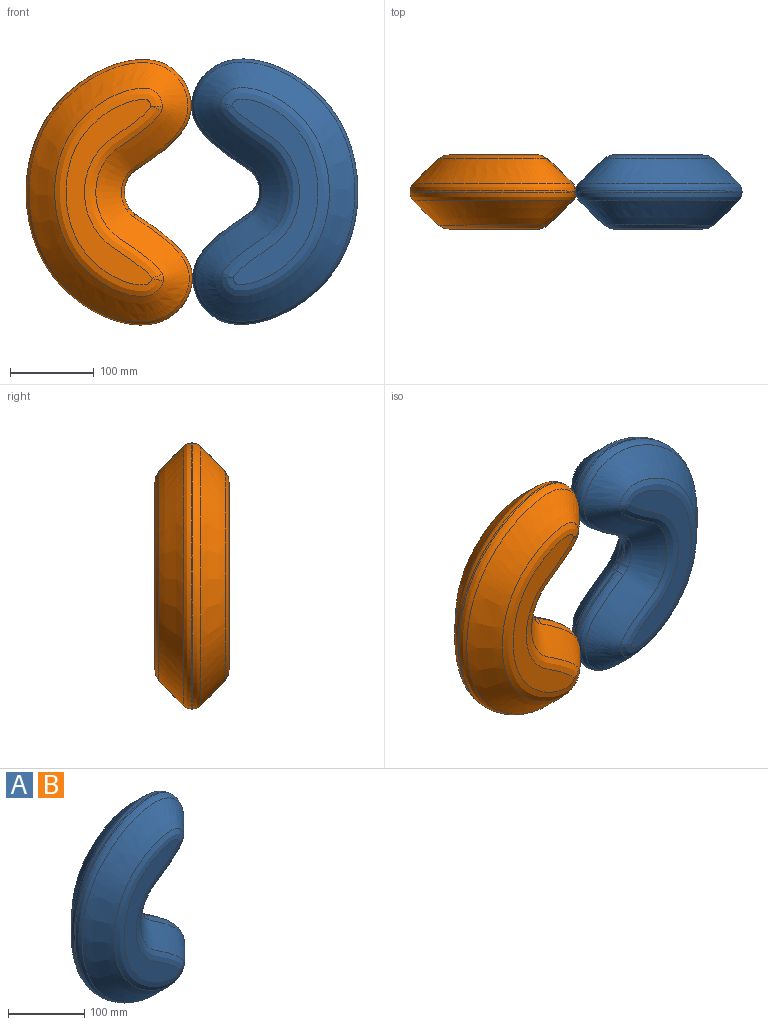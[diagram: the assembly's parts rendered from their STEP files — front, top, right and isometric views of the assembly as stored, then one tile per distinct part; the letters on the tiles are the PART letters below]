
ASSEMBLY  parts=2 mates=1
PART A: 24 faces, bbox 198.6x88.9x316.7 mm
  f0: plane 221.21x102.81mm, normal (0,-1,0), area 7218.9mm2, adj f3,f4
  f1: bspline ~309.04x190.25mm, area 33901.5mm2, adj f2,f3,f4,f5,f20,f21,f22,f23
  f2: bspline ~13.73x8.65mm, area 69mm2, adj f1,f3,f4
  f3: bspline ~206.74x93.09mm, area 3926.4mm2, adj f0,f1,f2,f5
  f4: bspline ~248.24x129.72mm, area 5664.5mm2, adj f0,f1,f2,f5
  f5: bspline ~13.51x5.1mm, area 25.1mm2, adj f1,f3,f4
  f6: cylinder r=25.4mm len=7.28mm, axis (0,-1,0), area 21.9mm2, adj f7,f9,f17,f22
  f7: extruded ~315.96x197.64mm, area 1742.8mm2, adj f6,f8,f16,f20
  f8: cylinder r=25.4mm len=7.32mm, axis (0,-1,0), area 22mm2, adj f7,f9,f18,f21
  f9: cylinder r=34.34mm len=37.54mm, axis (0,-1,0), area 84mm2, adj f6,f8,f19,f23
  f10: plane 221.21x102.81mm, normal (0,1,0), area 7218.9mm2, adj f13,f14
  f11: bspline ~309.04x190.25mm, area 33899.7mm2, adj f12,f13,f14,f15,f16,f17,f18,f19
  f12: bspline ~13.73x8.65mm, area 45.7mm2, adj f11,f13,f14
  f13: bspline ~206.74x93.09mm, area 3926.4mm2, adj f10,f11,f12,f15
  f14: bspline ~248.24x129.72mm, area 5664.5mm2, adj f10,f11,f12,f15
  f15: bspline ~13.51x5.1mm, area 25.1mm2, adj f11,f13,f14
  f16: bspline ~316.74x198.57mm, area 8514.5mm2, adj f7,f11,f17,f18
  f17: bspline ~12.15x11.88mm, area 108.8mm2, adj f6,f11,f16,f19
  f18: bspline ~12.17x11.9mm, area 109.4mm2, adj f8,f11,f16,f19
  f19: bspline ~42.66x9.85mm, area 412.7mm2, adj f9,f11,f17,f18
  f20: bspline ~316.74x198.57mm, area 8514.6mm2, adj f1,f7,f21,f22
  f21: bspline ~11.81x11.45mm, area 109.4mm2, adj f1,f8,f20,f23
  f22: bspline ~12.15x11.88mm, area 108.8mm2, adj f1,f6,f20,f23
  f23: bspline ~43.25x9.87mm, area 412.7mm2, adj f1,f9,f21,f22
PART B: same geometry as A
PLACE A rot(axis=(0,1,0),180deg) t=(247.66,36.96,21.55)mm
PLACE B t=(51.72,36.96,20.52)mm fixed
MATE planar A.f0 <-> B.f0  axis (0,-1,0) through (299.98,-1.14,21.6)mm
